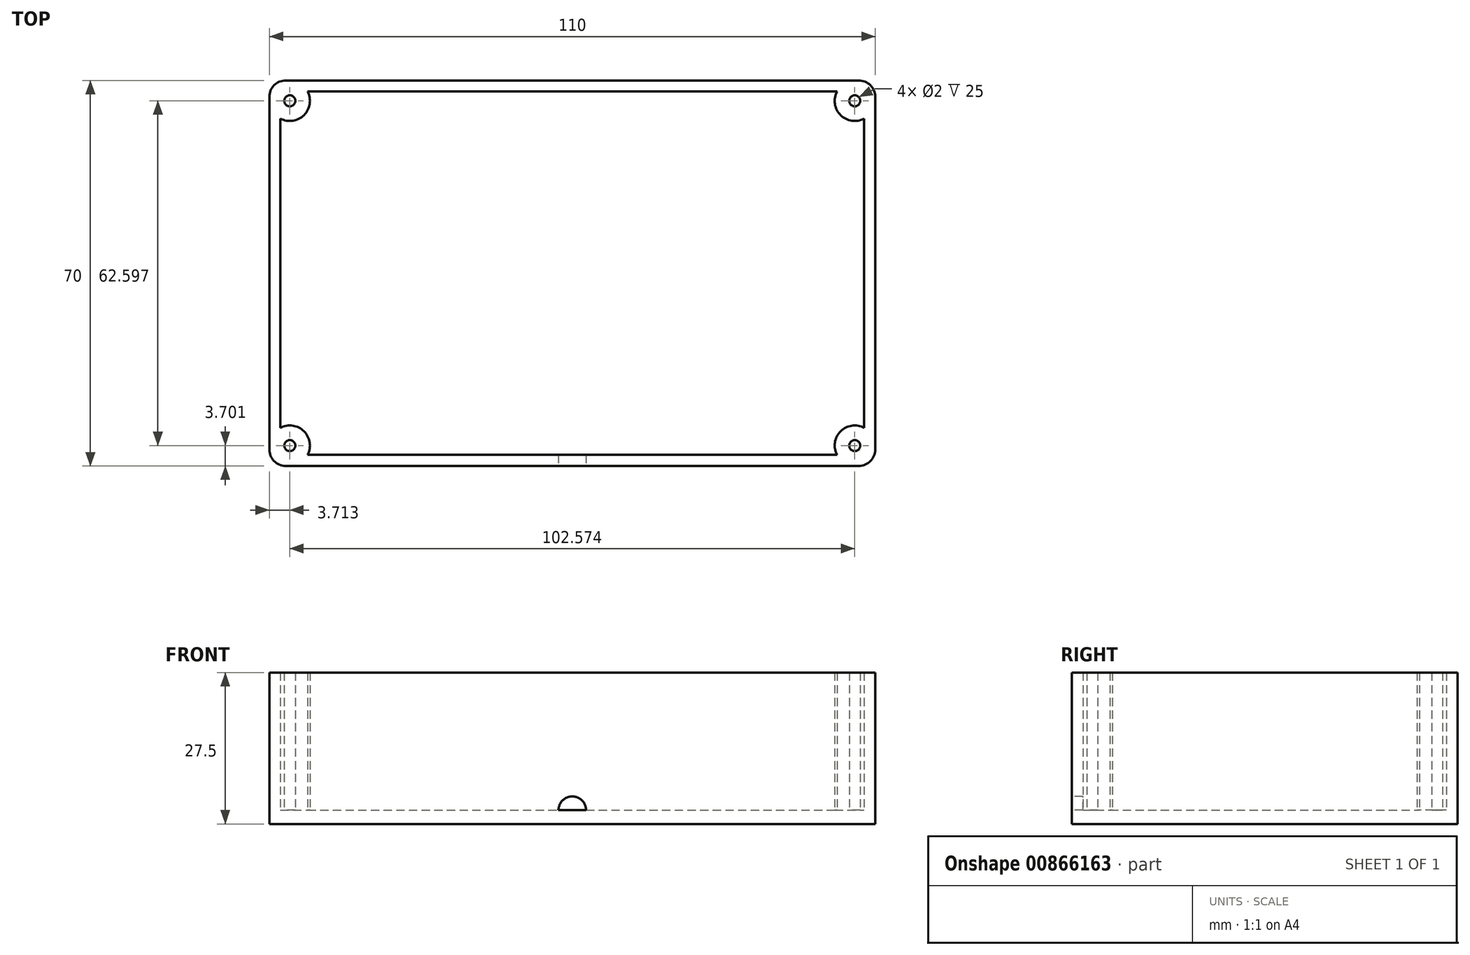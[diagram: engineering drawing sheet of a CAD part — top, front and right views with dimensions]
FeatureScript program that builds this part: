
annotation { "Feature Type Name" : "Feature", "Feature Type Description" : "" }
export const myFeature = defineFeature(function(context is Context, id is Id, definition is map)
    precondition{}
    {
        {
            var Q0;
            Q0=qCreatedBy(makeId("Top.planeOp"),FACE);
            var sketch = newSketch(context, id + "F0", { "sketchPlane" : qUnion([Q0])});
            skLineSegment(sketch, "E0.bottom", {"start": v(52, 35) * mm, "end": v(-52, 35) * mm});
            skLineSegment(sketch, "E0.top", {"start": v(52, -35) * mm, "end": v(-52, -35) * mm});
            skLineSegment(sketch, "E0.left", {"start": v(55, 32) * mm, "end": v(55, -32) * mm});
            skLineSegment(sketch, "E0.right", {"start": v(-55, 32) * mm, "end": v(-55, -32) * mm});
            skPoint(sketch, "E0.middle", {"position": v(0, 0) * mm});
            skPoint(sketch, "E1.visualSharp", {"position": v(-55, 35) * mm});
            skArc(sketch, "E1.filletArc", {"start": v(-52, 35) * mm, "mid": v(-54.12, 34.12) * mm, "end": v(-55, 32) * mm});
            skPoint(sketch, "E2.visualSharp", {"position": v(55, 35) * mm});
            skArc(sketch, "E2.filletArc", {"start": v(55, 32) * mm, "mid": v(54.12, 34.12) * mm, "end": v(52, 35) * mm});
            skPoint(sketch, "E3.visualSharp", {"position": v(-55, -35) * mm});
            skArc(sketch, "E3.filletArc", {"start": v(-55, -32) * mm, "mid": v(-54.12, -34.12) * mm, "end": v(-52, -35) * mm});
            skPoint(sketch, "E4.visualSharp", {"position": v(55, -35) * mm});
            skArc(sketch, "E4.filletArc", {"start": v(52, -35) * mm, "mid": v(54.12, -34.12) * mm, "end": v(55, -32) * mm});
            skLineSegment(sketch, "E5.0", {"start": v(53, 33) * mm, "end": v(-53, 33) * mm});
            skLineSegment(sketch, "E5.1", {"start": v(53, 33) * mm, "end": v(53, -33) * mm});
            skLineSegment(sketch, "E5.2", {"start": v(53, -33) * mm, "end": v(-53, -33) * mm});
            skLineSegment(sketch, "E5.3", {"start": v(-53, 33) * mm, "end": v(-53, -33) * mm});
            skPoint(sketch, "E6", {"position": v(-51.3, 31.3) * mm});
            skPoint(sketch, "E7.MirrorP", {"position": v(-51.3, -31.3) * mm});
            skPoint(sketch, "E8.MirrorP", {"position": v(51.3, -31.3) * mm});
            skPoint(sketch, "E9.MirrorP", {"position": v(51.3, 31.3) * mm});
            skSolve(sketch);
        }
        {
            var Q0;
            Q0=makeQuery(id+"F0.imprint","IMPRINT",FACE,{"disambiguationData":[TD([[makeQuery(id+"F0.imprint","IMPRINT",EDGE,{"derivedFrom":sQuery(id+"F0.wireOp",EDGE,"E0.bottom")}),1.0]])]});
            var Q1;
            Q1=makeQuery(id+"F0.imprint","IMPRINT",FACE,{"disambiguationData":[TD([[makeQuery(id+"F0.imprint","IMPRINT",EDGE,{"derivedFrom":sQuery(id+"F0.wireOp",EDGE,"E5.0")}),1.0]])]});
            extrude(context, id + "F1", {"entities" : qUnion([Q0, Q1]), "depth" : 2.5 * mm, "offsetDistance" : 25 * mm});
        }
        {
            var Q0;
            Q0=makeQuery(id+"F0.imprint","IMPRINT",FACE,{"disambiguationData":[TD([[makeQuery(id+"F0.imprint","IMPRINT",EDGE,{"derivedFrom":sQuery(id+"F0.wireOp",EDGE,"E0.bottom")}),1.0]])]});
            extrude(context, id + "F2", {"entities" : qUnion([Q0]), "operationType" : NewBodyOperationType.ADD, "depth" : 27.5 * mm, "offsetDistance" : 25 * mm});
        }
        {
            var Q0;
            Q0=makeQuery(id+"F1.opExtrude","CAP_FACE",FACE,{"disambiguationData":[OSD([sQuery(id+"F0.wireOp",EDGE,"E0.bottom"),sQuery(id+"F0.wireOp",EDGE,"E0.top"),sQuery(id+"F0.wireOp",EDGE,"E0.left"),sQuery(id+"F0.wireOp",EDGE,"E0.right"),sQuery(id+"F0.wireOp",EDGE,"E1.filletArc"),sQuery(id+"F0.wireOp",EDGE,"E2.filletArc"),sQuery(id+"F0.wireOp",EDGE,"E3.filletArc"),sQuery(id+"F0.wireOp",EDGE,"E4.filletArc")])],"isStart":false});
            var sketch = newSketch(context, id + "F3", { "sketchPlane" : qUnion([Q0])});
            skCircle(sketch, "E10", {"center": v(-51.29, 31.3) * mm, "radius": 3.65 * mm});
            skCircle(sketch, "E11.MirrorC", {"center": v(-51.29, -31.3) * mm, "radius": 3.65 * mm});
            skCircle(sketch, "E12.MirrorC", {"center": v(51.29, -31.3) * mm, "radius": 3.65 * mm});
            skCircle(sketch, "E13.MirrorC", {"center": v(51.29, 31.3) * mm, "radius": 3.65 * mm});
            skCircle(sketch, "E14.0", {"center": v(-51.29, 31.3) * mm, "radius": 1 * mm});
            skCircle(sketch, "E15.MirrorC", {"center": v(-51.29, -31.3) * mm, "radius": 1 * mm});
            skCircle(sketch, "E16.MirrorC", {"center": v(51.29, 31.3) * mm, "radius": 1 * mm});
            skCircle(sketch, "E17.MirrorC", {"center": v(51.29, -31.3) * mm, "radius": 1 * mm});
            skSolve(sketch);
        }
        {
            var Q0;
            Q0 = qSketchRegion(id + "F3", true);
            extrude(context, id + "F4", {"entities" : qUnion([Q0]), "operationType" : NewBodyOperationType.ADD, "depth" : 25 * mm, "offsetDistance" : 25 * mm});
        }
        {
            var Q0;
            Q0=qCreatedBy(makeId("Front.planeOp"),FACE);
            cPlane(context, id + "F5", {"entities" : qUnion([Q0]), "cplaneType" : CPlaneType.OFFSET, "offset" : 35 * mm, "width" : 150 * mm, "height" : 150 * mm});
        }
        {
            var Q0;
            Q0=qCreatedBy(id+"F5.planeOp",FACE);
            var sketch = newSketch(context, id + "F6", { "sketchPlane" : qUnion([Q0])});
            skArc(sketch, "E18", {"start": v(2.5, 2.5) * mm, "mid": v(0, 5) * mm, "end": v(-2.5, 2.5) * mm});
            skLineSegment(sketch, "E19", {"start": v(-2.5, 2.5) * mm, "end": v(2.5, 2.5) * mm});
            skSolve(sketch);
        }
        {
            var Q0;
            Q0=makeQuery(id+"F6.imprint","IMPRINT",FACE,{"disambiguationData":[TD([[makeQuery(id+"F6.imprint","IMPRINT",EDGE,{"derivedFrom":sQuery(id+"F6.wireOp",EDGE,"E18")}),1.0]])]});
            var Q1;
            Q1=makeQuery(id+"F2.opExtrude","SWEPT_FACE",FACE,{"disambiguationData":[OSD([sQuery(id+"F0.wireOp",EDGE,"E5.2")])]});
            var Q2;
            Q2=makeQuery(id+"F1.opExtrude","SWEPT_BODY",BODY,{"disambiguationData":[OSD([sQuery(id+"F0.wireOp",EDGE,"E0.bottom"),sQuery(id+"F0.wireOp",EDGE,"E0.top"),sQuery(id+"F0.wireOp",EDGE,"E0.left"),sQuery(id+"F0.wireOp",EDGE,"E0.right"),sQuery(id+"F0.wireOp",EDGE,"E1.filletArc"),sQuery(id+"F0.wireOp",EDGE,"E2.filletArc"),sQuery(id+"F0.wireOp",EDGE,"E3.filletArc"),sQuery(id+"F0.wireOp",EDGE,"E4.filletArc")])]});
            extrude(context, id + "F7", {"entities" : qUnion([Q0]), "operationType" : NewBodyOperationType.REMOVE, "endBound" : BoundingType.UP_TO_SURFACE, "oppositeDirection" : true, "depth" : 21 * mm, "endBoundEntityFace" : qUnion([Q1]), "endBoundEntityBody" : qUnion([Q2]), "offsetDistance" : 25 * mm});
        }
    });
